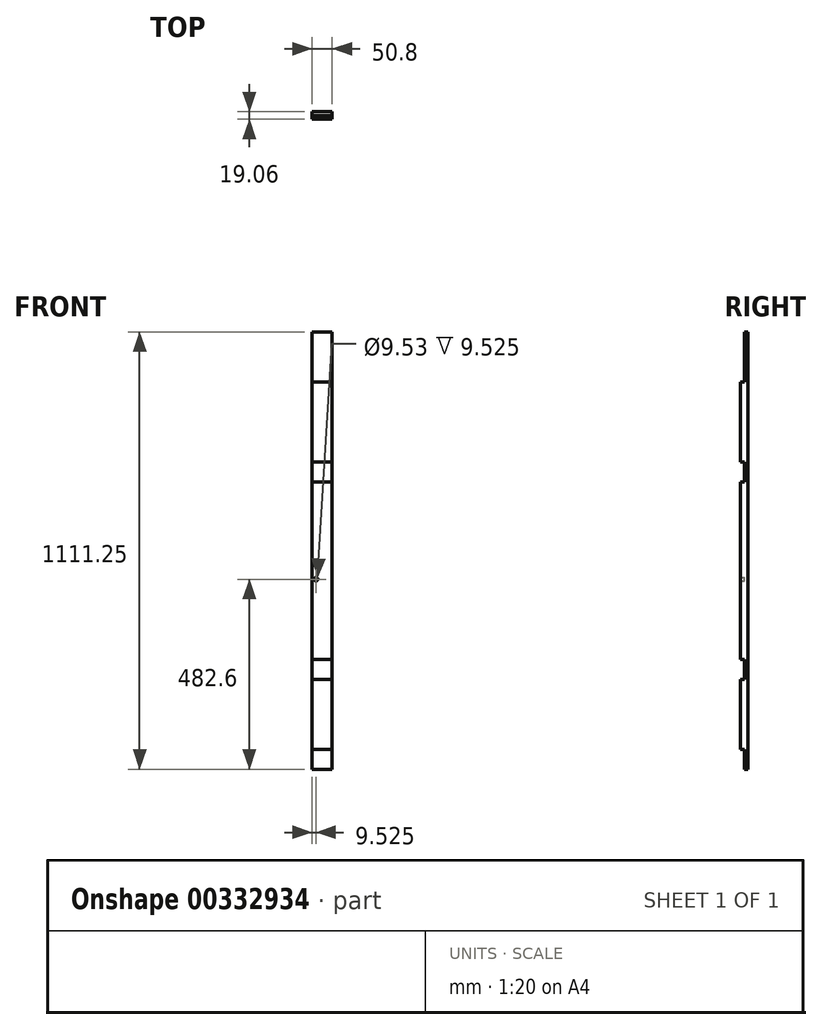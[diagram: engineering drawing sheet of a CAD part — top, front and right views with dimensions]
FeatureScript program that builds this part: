
annotation { "Feature Type Name" : "Feature", "Feature Type Description" : "" }
export const myFeature = defineFeature(function(context is Context, id is Id, definition is map)
    precondition{}
    {
        {
            var Q0;
            Q0=qCreatedBy(makeId("Top.planeOp"),FACE);
            var sketch = newSketch(context, id + "F0", { "sketchPlane" : qUnion([Q0])});
            skLineSegment(sketch, "E0.bottom", {"start": v(25.4, 9.53) * mm, "end": v(-25.4, 9.53) * mm});
            skLineSegment(sketch, "E0.top", {"start": v(25.4, -9.53) * mm, "end": v(-25.4, -9.53) * mm});
            skLineSegment(sketch, "E0.left", {"start": v(25.4, 9.53) * mm, "end": v(25.4, -9.52) * mm});
            skLineSegment(sketch, "E0.right", {"start": v(-25.4, 9.53) * mm, "end": v(-25.4, -9.53) * mm});
            skPoint(sketch, "E0.middle", {"position": v(0, 0) * mm});
            skSolve(sketch);
        }
        {
            var Q0;
            Q0=makeQuery(id+"F0.imprint","IMPRINT",FACE,{"disambiguationData":[TD([[makeQuery(id+"F0.imprint","IMPRINT",EDGE,{"derivedFrom":sQuery(id+"F0.wireOp",EDGE,"E0.bottom")}),1.0]])]});
            extrude(context, id + "F1", {"entities" : qUnion([Q0]), "depth" : 1111.25 * mm});
        }
        {
            var Q0;
            Q0=qCreatedBy(makeId("Front.planeOp"),FACE);
            var sketch = newSketch(context, id + "F2", { "sketchPlane" : qUnion([Q0])});
            skLineSegment(sketch, "E1.bottom", {"start": v(-38.77, 0) * mm, "end": v(83.66, 0) * mm});
            skLineSegment(sketch, "E1.top", {"start": v(-38.77, 50.8) * mm, "end": v(83.66, 50.8) * mm});
            skLineSegment(sketch, "E1.left", {"start": v(-38.77, 0) * mm, "end": v(-38.77, 50.8) * mm});
            skLineSegment(sketch, "E1.right", {"start": v(83.66, 0) * mm, "end": v(83.66, 50.8) * mm});
            skLineSegment(sketch, "E2.bottom", {"start": v(-44.21, 730.25) * mm, "end": v(49.65, 730.25) * mm});
            skLineSegment(sketch, "E2.top", {"start": v(-44.21, 781.05) * mm, "end": v(49.65, 781.05) * mm});
            skLineSegment(sketch, "E2.left", {"start": v(-44.21, 730.25) * mm, "end": v(-44.21, 781.05) * mm});
            skLineSegment(sketch, "E2.right", {"start": v(49.65, 730.25) * mm, "end": v(49.65, 781.05) * mm});
            skLineSegment(sketch, "E3.bottom", {"start": v(-210.36, 984.25) * mm, "end": v(132.8, 984.25) * mm});
            skLineSegment(sketch, "E3.top", {"start": v(-210.36, 1111.25) * mm, "end": v(132.8, 1111.25) * mm});
            skLineSegment(sketch, "E3.left", {"start": v(-210.36, 984.25) * mm, "end": v(-210.36, 1111.25) * mm});
            skLineSegment(sketch, "E3.right", {"start": v(132.8, 984.25) * mm, "end": v(132.8, 1111.25) * mm});
            skLineSegment(sketch, "E4.bottom", {"start": v(-145.57, 228.6) * mm, "end": v(93.98, 228.6) * mm});
            skLineSegment(sketch, "E4.top", {"start": v(-145.57, 279.4) * mm, "end": v(93.98, 279.4) * mm});
            skLineSegment(sketch, "E4.left", {"start": v(-145.57, 228.6) * mm, "end": v(-145.57, 279.4) * mm});
            skLineSegment(sketch, "E4.right", {"start": v(93.98, 228.6) * mm, "end": v(93.98, 279.4) * mm});
            skSolve(sketch);
        }
        {
            var Q0;
            Q0=qSketchRegion(id+"F2",true);
            extrude(context, id + "F3", {"entities" : qUnion([Q0]), "operationType" : NewBodyOperationType.REMOVE, "depth" : 25.4 * mm});
        }
        {
            var Q0;
            Q0=qCreatedBy(makeId("Front.planeOp"),FACE);
            var sketch = newSketch(context, id + "F4", { "sketchPlane" : qUnion([Q0])});
            skCircle(sketch, "E5", {"center": v(-15.88, 254) * mm, "radius": 4.76 * mm});
            skCircle(sketch, "E6", {"center": v(-15.88, 482.6) * mm, "radius": 4.76 * mm});
            skSolve(sketch);
        }
        {
            var Q0;
            Q0=qSketchRegion(id+"F4",true);
            extrude(context, id + "F5", {"entities" : qUnion([Q0]), "operationType" : NewBodyOperationType.REMOVE, "depth" : 25.4 * mm});
        }
    });
